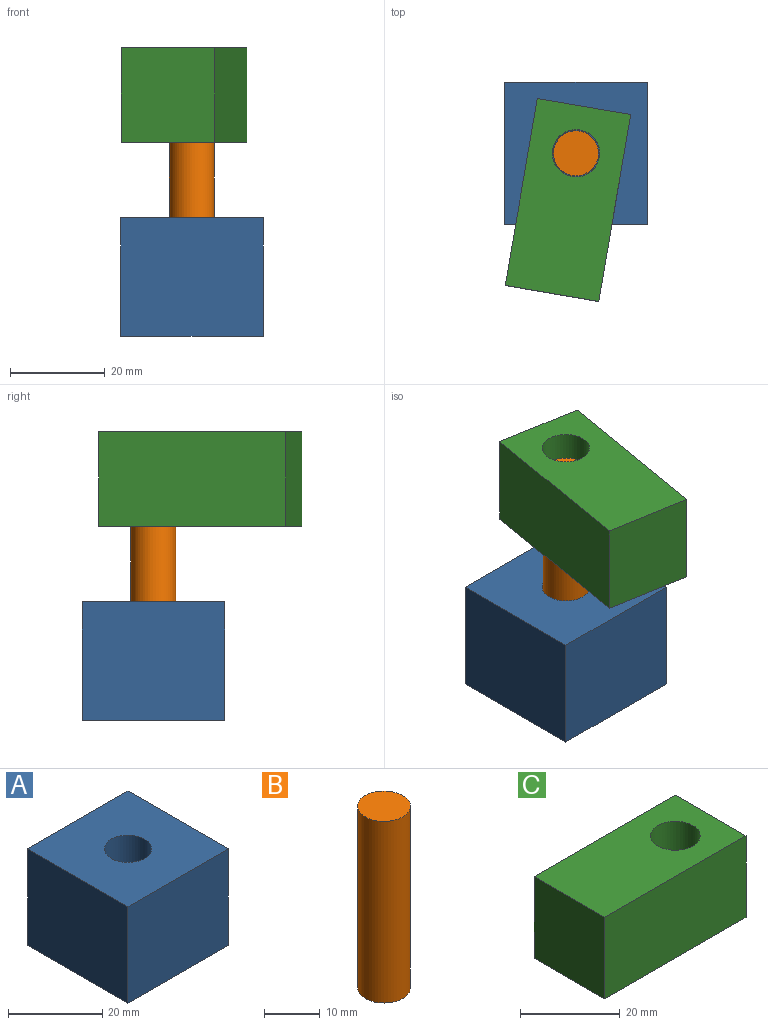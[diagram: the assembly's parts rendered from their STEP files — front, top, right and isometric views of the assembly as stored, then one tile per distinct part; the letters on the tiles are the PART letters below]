
ASSEMBLY  parts=3 mates=2
PART A: 8 faces, bbox 30x30x25 mm
  f0: plane 30x25mm, normal (-1,0,0), area 750mm2, adj f1,f3,f4,f5
  f1: plane 30x25mm, normal (0,-1,0), area 750mm2, adj f0,f2,f4,f5
  f2: plane 30x25mm, normal (1,0,0), area 750mm2, adj f1,f3,f4,f5
  f3: plane 30x25mm, normal (0,1,0), area 750mm2, adj f0,f2,f4,f5
  f4: plane 30x30mm, normal (0,0,1), area 821.5mm2, adj f0,f1,f2,f3,f6
  f5: plane 30x30mm, normal (0,0,-1), area 900mm2, adj f0,f1,f2,f3
  f6: cylinder r=5mm len=10mm, axis (0,0,1), area 314.2mm2, adj f4,f7
  f7: plane 10x10mm, normal (0,0,1), area 78.5mm2, adj f6
PART B: 3 faces, bbox 9.5x9.5x40 mm
  f0: cylinder r=4.75mm len=40mm, axis (0,0,-1), area 1193.8mm2, adj f1,f2
  f1: plane 9.5x9.5mm, normal (0,0,1), area 70.9mm2, adj f0
  f2: plane 9.5x9.5mm, normal (0,0,-1), area 70.9mm2, adj f0
PART C: 7 faces, bbox 40x20x20 mm
  f0: plane 20x20mm, normal (-1,0,0), area 400mm2, adj f1,f4,f5,f6
  f1: plane 40x20mm, normal (0,-1,0), area 800mm2, adj f0,f2,f5,f6
  f2: plane 20x20mm, normal (1,0,0), area 400mm2, adj f1,f4,f5,f6
  f3: cylinder r=5mm len=20mm, axis (0,0,-1), area 628.3mm2, adj f5,f6
  f4: plane 40x20mm, normal (0,1,0), area 800mm2, adj f0,f2,f5,f6
  f5: plane 40x20mm, normal (0,0,1), area 721.5mm2, adj f0,f1,f2,f3,f4
  f6: plane 40x20mm, normal (0,0,-1), area 721.5mm2, adj f0,f1,f2,f3,f4
PLACE A t=(-48.98,9.2,14.01)mm fixed
PLACE B rot(axis=(0,0,1),80.3deg) t=(19.17,17.21,29.01)mm
PLACE C rot(axis=(0,0,1),80.3deg) t=(-10.1,27.73,54.92)mm
MATE revolute B.f0 <-> A.f6  axis (0,0,-1) through (-10.1,27.73,29.01)mm
MATE slider B.f0 <-> C.f3  axis (0,0,-1) through (-10.1,27.73,69.01)mm
